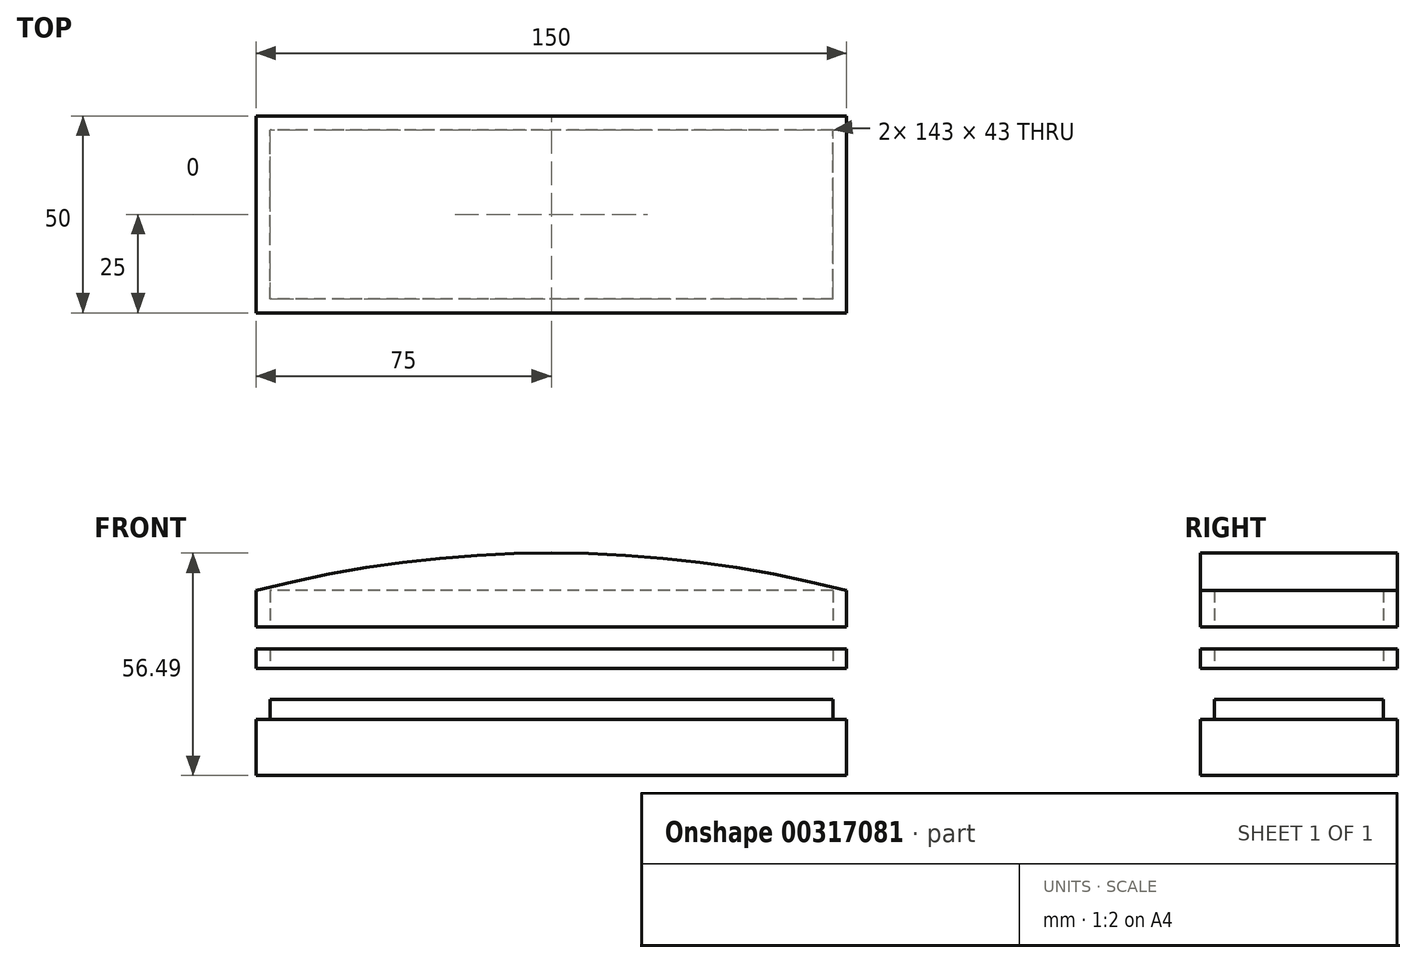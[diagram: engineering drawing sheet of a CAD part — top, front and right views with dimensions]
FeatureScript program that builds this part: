
annotation { "Feature Type Name" : "Feature", "Feature Type Description" : "" }
export const myFeature = defineFeature(function(context is Context, id is Id, definition is map)
    precondition{}
    {
        {
            var Q0;
            Q0=qCreatedBy(makeId("Front.planeOp"),FACE);
            var sketch = newSketch(context, id + "F0", { "sketchPlane" : qUnion([Q0])});
            skLineSegment(sketch, "E0.bottom", {"start": v(75, 7.13) * mm, "end": v(-75, 7.13) * mm});
            skLineSegment(sketch, "E0.top", {"start": v(75, -7.14) * mm, "end": v(-75, -7.14) * mm});
            skLineSegment(sketch, "E0.left", {"start": v(75, 7.13) * mm, "end": v(75, -7.13) * mm});
            skLineSegment(sketch, "E0.right", {"start": v(-75, 7.13) * mm, "end": v(-75, -7.14) * mm});
            skPoint(sketch, "E0.middle", {"position": v(0, 0) * mm});
            skSolve(sketch);
        }
        {
            var Q0;
            Q0 = qSketchRegion(id + "F0", true);
            extrude(context, id + "F1", {"entities" : qUnion([Q0]), "depth" : 25 * mm});
        }
        {
            var Q0;
            Q0=makeQuery(id+"F1.opExtrude","CAP_FACE",FACE,{"disambiguationData":[OSD([sQuery(id+"F0.wireOp",EDGE,"E0.bottom"),sQuery(id+"F0.wireOp",EDGE,"E0.top"),sQuery(id+"F0.wireOp",EDGE,"E0.left"),sQuery(id+"F0.wireOp",EDGE,"E0.right")])],"isStart":true});
            extrude(context, id + "F2", {"entities" : qUnion([Q0]), "operationType" : NewBodyOperationType.ADD, "depth" : 25 * mm});
        }
        {
            var Q0;
            {var subQ0=sQuery(id+"F0.wireOp",EDGE,"E0.top");Q0=makeQuery(id+"F2.boolean.opBoolean","MERGE",FACE,{"derivedFrom":[makeQuery(id+"F1.opExtrude","SWEPT_FACE",FACE,{"disambiguationData":[OSD([subQ0])]}),makeQuery(id+"F2.opExtrude","SWEPT_FACE",FACE,{"disambiguationData":[OSD([subQ0])]})]});}
            var sketch = newSketch(context, id + "F3", { "sketchPlane" : qUnion([Q0])});
            skLineSegment(sketch, "E1.bottom", {"start": v(-71.5, -21.5) * mm, "end": v(71.5, -21.5) * mm});
            skLineSegment(sketch, "E1.top", {"start": v(-71.5, 21.5) * mm, "end": v(71.5, 21.5) * mm});
            skLineSegment(sketch, "E1.left", {"start": v(-71.5, -21.5) * mm, "end": v(-71.5, 21.5) * mm});
            skLineSegment(sketch, "E1.right", {"start": v(71.5, -21.5) * mm, "end": v(71.5, 21.5) * mm});
            skPoint(sketch, "E1.middle", {"position": v(0, 0) * mm});
            skSolve(sketch);
        }
        {
            var Q0;
            Q0 = qSketchRegion(id + "F3", true);
            extrude(context, id + "F4", {"entities" : qUnion([Q0]), "operationType" : NewBodyOperationType.ADD, "oppositeDirection" : true, "depth" : 19.27 * mm});
        }
        {
            var Q0;
            Q0=qCreatedBy(makeId("Top.planeOp"),FACE);
            cPlane(context, id + "F5", {"entities" : qUnion([Q0]), "cplaneType" : CPlaneType.OFFSET, "offset" : 20 * mm, "width" : 150 * mm, "height" : 150 * mm});
        }
        {
            var Q0;
            Q0=qCreatedBy(id+"F5.planeOp",FACE);
            var sketch = newSketch(context, id + "F6", { "sketchPlane" : qUnion([Q0])});
            skLineSegment(sketch, "E2.bottom", {"start": v(75, 25) * mm, "end": v(-75, 25) * mm});
            skLineSegment(sketch, "E2.top", {"start": v(75, -25) * mm, "end": v(-75, -25) * mm});
            skLineSegment(sketch, "E2.left", {"start": v(75, 25) * mm, "end": v(75, -25) * mm});
            skLineSegment(sketch, "E2.right", {"start": v(-75, 25) * mm, "end": v(-75, -25) * mm});
            skPoint(sketch, "E2.middle", {"position": v(0, 0) * mm});
            skLineSegment(sketch, "E3.bottom", {"start": v(71.5, 21.5) * mm, "end": v(-71.5, 21.5) * mm});
            skLineSegment(sketch, "E3.top", {"start": v(71.5, -21.5) * mm, "end": v(-71.5, -21.5) * mm});
            skLineSegment(sketch, "E3.left", {"start": v(71.5, 21.5) * mm, "end": v(71.5, -21.5) * mm});
            skLineSegment(sketch, "E3.right", {"start": v(-71.5, 21.5) * mm, "end": v(-71.5, -21.5) * mm});
            skSolve(sketch);
        }
        {
            var Q0;
            Q0=makeQuery(id+"F6.imprint","IMPRINT",FACE,{"disambiguationData":[TD([[makeQuery(id+"F6.imprint","IMPRINT",EDGE,{"derivedFrom":sQuery(id+"F6.wireOp",EDGE,"E2.bottom")}),1.0]])]});
            extrude(context, id + "F7", {"entities" : qUnion([Q0]), "depth" : 5 * mm});
        }
        {
            var Q0;
            Q0=qCreatedBy(makeId("Front.planeOp"),FACE);
            var sketch = newSketch(context, id + "F8", { "sketchPlane" : qUnion([Q0])});
            skLineSegment(sketch, "E4.bottom", {"start": v(75, 39.83) * mm, "end": v(-75, 39.83) * mm});
            skLineSegment(sketch, "E4.top", {"start": v(75, 30.56) * mm, "end": v(-75, 30.56) * mm});
            skLineSegment(sketch, "E4.left", {"start": v(75, 39.83) * mm, "end": v(75, 30.56) * mm});
            skLineSegment(sketch, "E4.right", {"start": v(-75, 39.83) * mm, "end": v(-75, 30.56) * mm});
            skPoint(sketch, "E4.middle", {"position": v(0, 35.2) * mm});
            skArc(sketch, "E5", {"start": v(75, 39.83) * mm, "mid": v(0, 49.36) * mm, "end": v(-75, 39.83) * mm});
            skSolve(sketch);
        }
        {
            var Q0;
            Q0=makeQuery(id+"F8.imprint","IMPRINT",FACE,{"disambiguationData":[TD([[makeQuery(id+"F8.imprint","IMPRINT",EDGE,{"derivedFrom":sQuery(id+"F8.wireOp",EDGE,"E4.bottom")}),-1.0]])]});
            var Q1;
            Q1=makeQuery(id+"F8.imprint","IMPRINT",FACE,{"disambiguationData":[TD([[makeQuery(id+"F8.imprint","IMPRINT",EDGE,{"derivedFrom":sQuery(id+"F8.wireOp",EDGE,"E4.bottom")}),1.0]])]});
            extrude(context, id + "F9", {"entities" : qUnion([Q0, Q1]), "depth" : 25 * mm});
        }
        {
            var Q0;
            Q0=makeQuery(id+"F9.opExtrude","CAP_FACE",FACE,{"disambiguationData":[OSD([sQuery(id+"F8.wireOp",EDGE,"E4.top"),sQuery(id+"F8.wireOp",EDGE,"E4.left"),sQuery(id+"F8.wireOp",EDGE,"E4.right"),sQuery(id+"F8.wireOp",EDGE,"E5")])],"isStart":true});
            extrude(context, id + "F10", {"entities" : qUnion([Q0]), "operationType" : NewBodyOperationType.ADD, "depth" : 25 * mm});
        }
        {
            var Q0;
            {var subQ0=sQuery(id+"F8.wireOp",EDGE,"E4.top");Q0=makeQuery(id+"F10.boolean.opBoolean","MERGE",FACE,{"derivedFrom":[makeQuery(id+"F9.opExtrude","SWEPT_FACE",FACE,{"disambiguationData":[OSD([subQ0])]}),makeQuery(id+"F10.opExtrude","SWEPT_FACE",FACE,{"disambiguationData":[OSD([subQ0])]})]});}
            var sketch = newSketch(context, id + "F11", { "sketchPlane" : qUnion([Q0])});
            skLineSegment(sketch, "E6.bottom", {"start": v(71.5, 21.5) * mm, "end": v(-71.5, 21.5) * mm});
            skLineSegment(sketch, "E6.top", {"start": v(71.5, -21.5) * mm, "end": v(-71.5, -21.5) * mm});
            skLineSegment(sketch, "E6.left", {"start": v(71.5, 21.5) * mm, "end": v(71.5, -21.5) * mm});
            skLineSegment(sketch, "E6.right", {"start": v(-71.5, 21.5) * mm, "end": v(-71.5, -21.5) * mm});
            skPoint(sketch, "E6.middle", {"position": v(0, 0) * mm});
            skSolve(sketch);
        }
        {
            var Q0;
            Q0=makeQuery(id+"F11.imprint","IMPRINT",FACE,{"disambiguationData":[TD([[makeQuery(id+"F11.imprint","IMPRINT",EDGE,{"derivedFrom":sQuery(id+"F11.wireOp",EDGE,"E6.bottom")}),1.0]])]});
            extrude(context, id + "F12", {"entities" : qUnion([Q0]), "operationType" : NewBodyOperationType.REMOVE, "oppositeDirection" : true, "depth" : 9.27 * mm});
        }
    });
